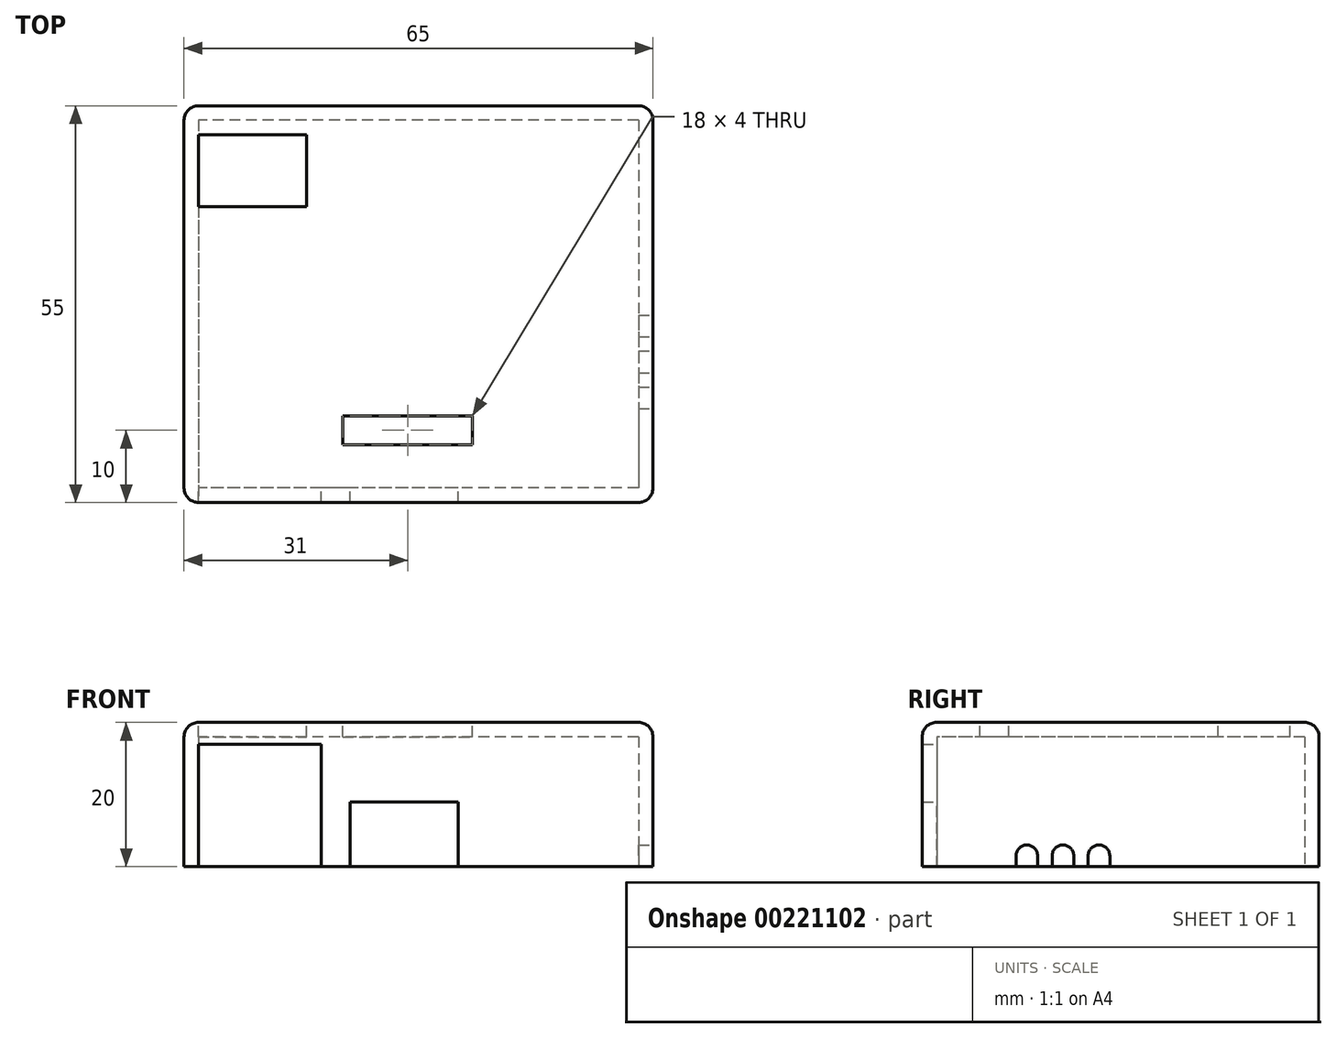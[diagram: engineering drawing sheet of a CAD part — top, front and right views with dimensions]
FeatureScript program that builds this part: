
annotation { "Feature Type Name" : "Feature", "Feature Type Description" : "" }
export const myFeature = defineFeature(function(context is Context, id is Id, definition is map)
    precondition{}
    {
        {
            var Q0;
            Q0=qCreatedBy(makeId("Top.planeOp"),FACE);
            var sketch = newSketch(context, id + "F0", { "sketchPlane" : qUnion([Q0])});
            skLineSegment(sketch, "E0.bottom", {"start": v(32.5, 27.5) * mm, "end": v(-32.5, 27.5) * mm});
            skLineSegment(sketch, "E0.top", {"start": v(32.5, -27.5) * mm, "end": v(-32.5, -27.5) * mm});
            skLineSegment(sketch, "E0.left", {"start": v(32.5, 27.5) * mm, "end": v(32.5, -27.5) * mm});
            skLineSegment(sketch, "E0.right", {"start": v(-32.5, 27.5) * mm, "end": v(-32.5, -27.5) * mm});
            skPoint(sketch, "E0.middle", {"position": v(0, 0) * mm});
            skSolve(sketch);
        }
        {
            var Q0;
            Q0=makeQuery(id+"F0.imprint","IMPRINT",FACE,{"disambiguationData":[TD([[makeQuery(id+"F0.imprint","IMPRINT",EDGE,{"derivedFrom":sQuery(id+"F0.wireOp",EDGE,"E0.bottom")}),1.0]])]});
            extrude(context, id + "F1", {"entities" : qUnion([Q0]), "endBound" : BoundingType.SYMMETRIC, "depth" : 20 * mm});
        }
        {
            var Q0;
            Q0=makeQuery(id+"F1.opExtrude","CAP_FACE",FACE,{"disambiguationData":[OSD([sQuery(id+"F0.wireOp",EDGE,"E0.bottom"),sQuery(id+"F0.wireOp",EDGE,"E0.top"),sQuery(id+"F0.wireOp",EDGE,"E0.left"),sQuery(id+"F0.wireOp",EDGE,"E0.right")])],"isStart":true});
            shell(context, id + "F2", {"entities" : qUnion([Q0]), "thickness" : 2 * mm});
        }
        {
            var Q0;
            Q0=qCreatedBy(makeId("Front.planeOp"),FACE);
            var sketch = newSketch(context, id + "F3", { "sketchPlane" : qUnion([Q0])});
            skLineSegment(sketch, "E1.bottom", {"start": v(-30.5, -10) * mm, "end": v(-13.5, -10) * mm});
            skLineSegment(sketch, "E1.top", {"start": v(-30.5, 7) * mm, "end": v(-13.5, 7) * mm});
            skLineSegment(sketch, "E1.left", {"start": v(-30.5, -10) * mm, "end": v(-30.5, 7) * mm});
            skLineSegment(sketch, "E1.right", {"start": v(-13.5, -10) * mm, "end": v(-13.5, 7) * mm});
            skLineSegment(sketch, "E2.bottom", {"start": v(-9.5, -1) * mm, "end": v(5.5, -1) * mm});
            skLineSegment(sketch, "E2.top", {"start": v(-9.5, -10) * mm, "end": v(5.5, -10) * mm});
            skLineSegment(sketch, "E2.left", {"start": v(-9.5, -1) * mm, "end": v(-9.5, -10) * mm});
            skLineSegment(sketch, "E2.right", {"start": v(5.5, -1) * mm, "end": v(5.5, -10) * mm});
            skSolve(sketch);
        }
        {
            var Q0;
            Q0 = qSketchRegion(id + "F3", true);
            var Q1;
            Q1=makeQuery(id+"F1.opExtrude","SWEPT_FACE",FACE,{"disambiguationData":[OSD([sQuery(id+"F0.wireOp",EDGE,"E0.top")])]});
            extrude(context, id + "F4", {"entities" : qUnion([Q0]), "operationType" : NewBodyOperationType.REMOVE, "endBound" : BoundingType.UP_TO_SURFACE, "endBoundEntityFace" : qUnion([Q1]), "depth" : 25.4 * mm});
        }
        {
            var Q0;
            Q0=makeQuery(id+"F1.opExtrude","SWEPT_FACE",FACE,{"disambiguationData":[OSD([sQuery(id+"F0.wireOp",EDGE,"E0.left")])]});
            var sketch = newSketch(context, id + "F5", { "sketchPlane" : qUnion([Q0])});
            skCircle(sketch, "E3", {"center": v(-13, -8.5) * mm, "radius": 1.5 * mm});
            skCircle(sketch, "E4", {"center": v(-8, -8.5) * mm, "radius": 1.5 * mm});
            skCircle(sketch, "E5", {"center": v(-3, -8.5) * mm, "radius": 1.5 * mm});
            skLineSegment(sketch, "E6", {"start": v(-14.5, -8.5) * mm, "end": v(-14.5, -10) * mm});
            skLineSegment(sketch, "E7", {"start": v(-11.5, -8.48) * mm, "end": v(-11.48, -10) * mm});
            skLineSegment(sketch, "E8", {"start": v(-14.5, -10) * mm, "end": v(-11.48, -10) * mm});
            skLineSegment(sketch, "E9", {"start": v(-9.5, -8.5) * mm, "end": v(-9.5, -10) * mm});
            skLineSegment(sketch, "E10", {"start": v(-4.5, -8.5) * mm, "end": v(-4.5, -10) * mm});
            skLineSegment(sketch, "E11", {"start": v(-1.5, -8.5) * mm, "end": v(-1.5, -10) * mm});
            skLineSegment(sketch, "E12", {"start": v(-1.5, -10) * mm, "end": v(-4.5, -10) * mm});
            skLineSegment(sketch, "E13", {"start": v(-6.5, -8.5) * mm, "end": v(-6.5, -10) * mm});
            skLineSegment(sketch, "E14", {"start": v(-9.5, -10) * mm, "end": v(-6.5, -10) * mm});
            skSolve(sketch);
        }
        {
            var Q0;
            {var subQ0=sQuery(id+"F5.wireOp",EDGE,"E6");Q0=makeQuery(id+"F5.imprint","IMPRINT",FACE,{"disambiguationData":[TD([[makeQuery(id+"F5.imprint","IMPRINT",EDGE,{"derivedFrom":subQ0}),1.0]])]});}
            var Q1;
            {var subQ0=sQuery(id+"F5.wireOp",EDGE,"E7");var subQ1=sQuery(id+"F5.wireOp",EDGE,"E3");var subQ2=makeQuery(id+"F5.imprint","INTERSECT",VERTEX,{"disambiguationData":[OD(0.0)],"derivedFrom":[subQ1,subQ0]});Q1=makeQuery(id+"F5.imprint","IMPRINT",FACE,{"disambiguationData":[TD([[makeQuery(id+"F5.imprint","IMPRINT",EDGE,{"disambiguationData":[TD([[subQ2,1.0]])],"derivedFrom":subQ1}),1.0]])]});}
            var Q2;
            {var subQ0=sQuery(id+"F5.wireOp",EDGE,"E8");var subQ1=sQuery(id+"F5.wireOp",EDGE,"E3");var subQ2=makeQuery(id+"F5.imprint","INTERSECT",VERTEX,{"derivedFrom":[subQ1,subQ0]});Q2=makeQuery(id+"F5.imprint","IMPRINT",FACE,{"disambiguationData":[TD([[makeQuery(id+"F5.imprint","IMPRINT",EDGE,{"disambiguationData":[TD([[subQ2,-1.0]])],"derivedFrom":subQ1}),-1.0]])]});}
            var Q3;
            {var subQ0=sQuery(id+"F5.wireOp",EDGE,"E4");var subQ1=makeQuery(id+"F5.imprint","INTERSECT",VERTEX,{"derivedFrom":[subQ0,sQuery(id+"F5.wireOp",EDGE,"E9")]});Q3=makeQuery(id+"F5.imprint","IMPRINT",FACE,{"disambiguationData":[TD([[makeQuery(id+"F5.imprint","IMPRINT",EDGE,{"disambiguationData":[TD([[subQ1,-1.0]])],"derivedFrom":subQ0}),1.0]])]});}
            var Q4;
            {var subQ0=sQuery(id+"F5.wireOp",EDGE,"E9");Q4=makeQuery(id+"F5.imprint","IMPRINT",FACE,{"disambiguationData":[TD([[makeQuery(id+"F5.imprint","IMPRINT",EDGE,{"derivedFrom":subQ0}),1.0]])]});}
            var Q5;
            {var subQ0=sQuery(id+"F5.wireOp",EDGE,"E13");Q5=makeQuery(id+"F5.imprint","IMPRINT",FACE,{"disambiguationData":[TD([[makeQuery(id+"F5.imprint","IMPRINT",EDGE,{"derivedFrom":subQ0}),-1.0]])]});}
            var Q6;
            {var subQ0=sQuery(id+"F5.wireOp",EDGE,"E5");var subQ1=makeQuery(id+"F5.imprint","INTERSECT",VERTEX,{"derivedFrom":[subQ0,sQuery(id+"F5.wireOp",EDGE,"E10")]});Q6=makeQuery(id+"F5.imprint","IMPRINT",FACE,{"disambiguationData":[TD([[makeQuery(id+"F5.imprint","IMPRINT",EDGE,{"disambiguationData":[TD([[subQ1,1.0]])],"derivedFrom":subQ0}),1.0]])]});}
            var Q7;
            {var subQ0=sQuery(id+"F5.wireOp",EDGE,"E10");Q7=makeQuery(id+"F5.imprint","IMPRINT",FACE,{"disambiguationData":[TD([[makeQuery(id+"F5.imprint","IMPRINT",EDGE,{"derivedFrom":subQ0}),1.0]])]});}
            var Q8;
            {var subQ0=sQuery(id+"F5.wireOp",EDGE,"E11");Q8=makeQuery(id+"F5.imprint","IMPRINT",FACE,{"disambiguationData":[TD([[makeQuery(id+"F5.imprint","IMPRINT",EDGE,{"derivedFrom":subQ0}),-1.0]])]});}
            var Q9;
            Q9=sQuery(id+"F5.wireOp",EDGE,"E8");
            var Q10;
            Q10=sQuery(id+"F5.wireOp",EDGE,"E6");
            var Q11;
            Q11=sQuery(id+"F5.wireOp",EDGE,"E3");
            var Q12;
            Q12=sQuery(id+"F5.wireOp",EDGE,"E7");
            extrude(context, id + "F6", {"entities" : qUnion([Q0, Q1, Q2, Q3, Q4, Q5, Q6, Q7, Q8]), "operationType" : NewBodyOperationType.REMOVE, "surfaceEntities" : qUnion([Q9, Q10, Q11, Q12]), "oppositeDirection" : true, "depth" : 25.4 * mm});
        }
        {
            var Q0;
            Q0=makeQuery(id+"F1.opExtrude","CAP_FACE",FACE,{"disambiguationData":[OSD([sQuery(id+"F0.wireOp",EDGE,"E0.bottom"),sQuery(id+"F0.wireOp",EDGE,"E0.top"),sQuery(id+"F0.wireOp",EDGE,"E0.left"),sQuery(id+"F0.wireOp",EDGE,"E0.right")])],"isStart":false});
            var sketch = newSketch(context, id + "F7", { "sketchPlane" : qUnion([Q0])});
            skLineSegment(sketch, "E15.bottom", {"start": v(-10.5, -15.5) * mm, "end": v(7.5, -15.5) * mm});
            skLineSegment(sketch, "E15.top", {"start": v(-10.5, -19.5) * mm, "end": v(7.5, -19.5) * mm});
            skLineSegment(sketch, "E15.left", {"start": v(-10.5, -15.5) * mm, "end": v(-10.5, -19.5) * mm});
            skLineSegment(sketch, "E15.right", {"start": v(7.5, -15.5) * mm, "end": v(7.5, -19.5) * mm});
            skLineSegment(sketch, "E16.bottom", {"start": v(-30.5, 23.5) * mm, "end": v(-15.5, 23.5) * mm});
            skLineSegment(sketch, "E16.top", {"start": v(-30.5, 13.5) * mm, "end": v(-15.5, 13.5) * mm});
            skLineSegment(sketch, "E16.left", {"start": v(-30.5, 23.5) * mm, "end": v(-30.5, 13.5) * mm});
            skLineSegment(sketch, "E16.right", {"start": v(-15.5, 23.5) * mm, "end": v(-15.5, 13.5) * mm});
            skSolve(sketch);
        }
        {
            var Q0;
            Q0=makeQuery(id+"F7.imprint","IMPRINT",FACE,{"disambiguationData":[TD([[makeQuery(id+"F7.imprint","IMPRINT",EDGE,{"derivedFrom":sQuery(id+"F7.wireOp",EDGE,"E16.bottom")}),-1.0]])]});
            var Q1;
            Q1=makeQuery(id+"F7.imprint","IMPRINT",FACE,{"disambiguationData":[TD([[makeQuery(id+"F7.imprint","IMPRINT",EDGE,{"derivedFrom":sQuery(id+"F7.wireOp",EDGE,"E15.bottom")}),-1.0]])]});
            extrude(context, id + "F8", {"entities" : qUnion([Q0, Q1]), "operationType" : NewBodyOperationType.REMOVE, "endBound" : BoundingType.SYMMETRIC, "oppositeDirection" : true, "depth" : 25.4 * mm});
        }
        {
            var Q0;
            Q0=makeQuery(id+"F1.opExtrude","SWEPT_EDGE",EDGE,{"disambiguationData":[OSD([sQuery(id+"F0.wireOp",EDGE,"E0.top"),sQuery(id+"F0.wireOp",EDGE,"E0.right")])]});
            var Q1;
            Q1=makeQuery(id+"F1.opExtrude","SWEPT_EDGE",EDGE,{"disambiguationData":[OSD([sQuery(id+"F0.wireOp",EDGE,"E0.top"),sQuery(id+"F0.wireOp",EDGE,"E0.left")])]});
            var Q2;
            Q2=makeQuery(id+"F1.opExtrude","SWEPT_EDGE",EDGE,{"disambiguationData":[OSD([sQuery(id+"F0.wireOp",EDGE,"E0.bottom"),sQuery(id+"F0.wireOp",EDGE,"E0.left")])]});
            var Q3;
            Q3=makeQuery(id+"F1.opExtrude","SWEPT_EDGE",EDGE,{"disambiguationData":[OSD([sQuery(id+"F0.wireOp",EDGE,"E0.bottom"),sQuery(id+"F0.wireOp",EDGE,"E0.right")])]});
            var Q4;
            Q4=makeQuery(id+"F1.opExtrude","CAP_EDGE",EDGE,{"disambiguationData":[OSD([sQuery(id+"F0.wireOp",EDGE,"E0.top")])],"isStart":false});
            var Q5;
            Q5=makeQuery(id+"F1.opExtrude","CAP_EDGE",EDGE,{"disambiguationData":[OSD([sQuery(id+"F0.wireOp",EDGE,"E0.left")])],"isStart":false});
            var Q6;
            Q6=makeQuery(id+"F1.opExtrude","CAP_EDGE",EDGE,{"disambiguationData":[OSD([sQuery(id+"F0.wireOp",EDGE,"E0.bottom")])],"isStart":false});
            var Q7;
            Q7=makeQuery(id+"F1.opExtrude","CAP_EDGE",EDGE,{"disambiguationData":[OSD([sQuery(id+"F0.wireOp",EDGE,"E0.right")])],"isStart":false});
            fillet(context, id + "F9", {"entities" : qUnion([Q0, Q1, Q2, Q3, Q4, Q5, Q6, Q7]), "radius" : 2 * mm, "tangentPropagation" : true, "allowEdgeOverflow" : false});
        }
    });
